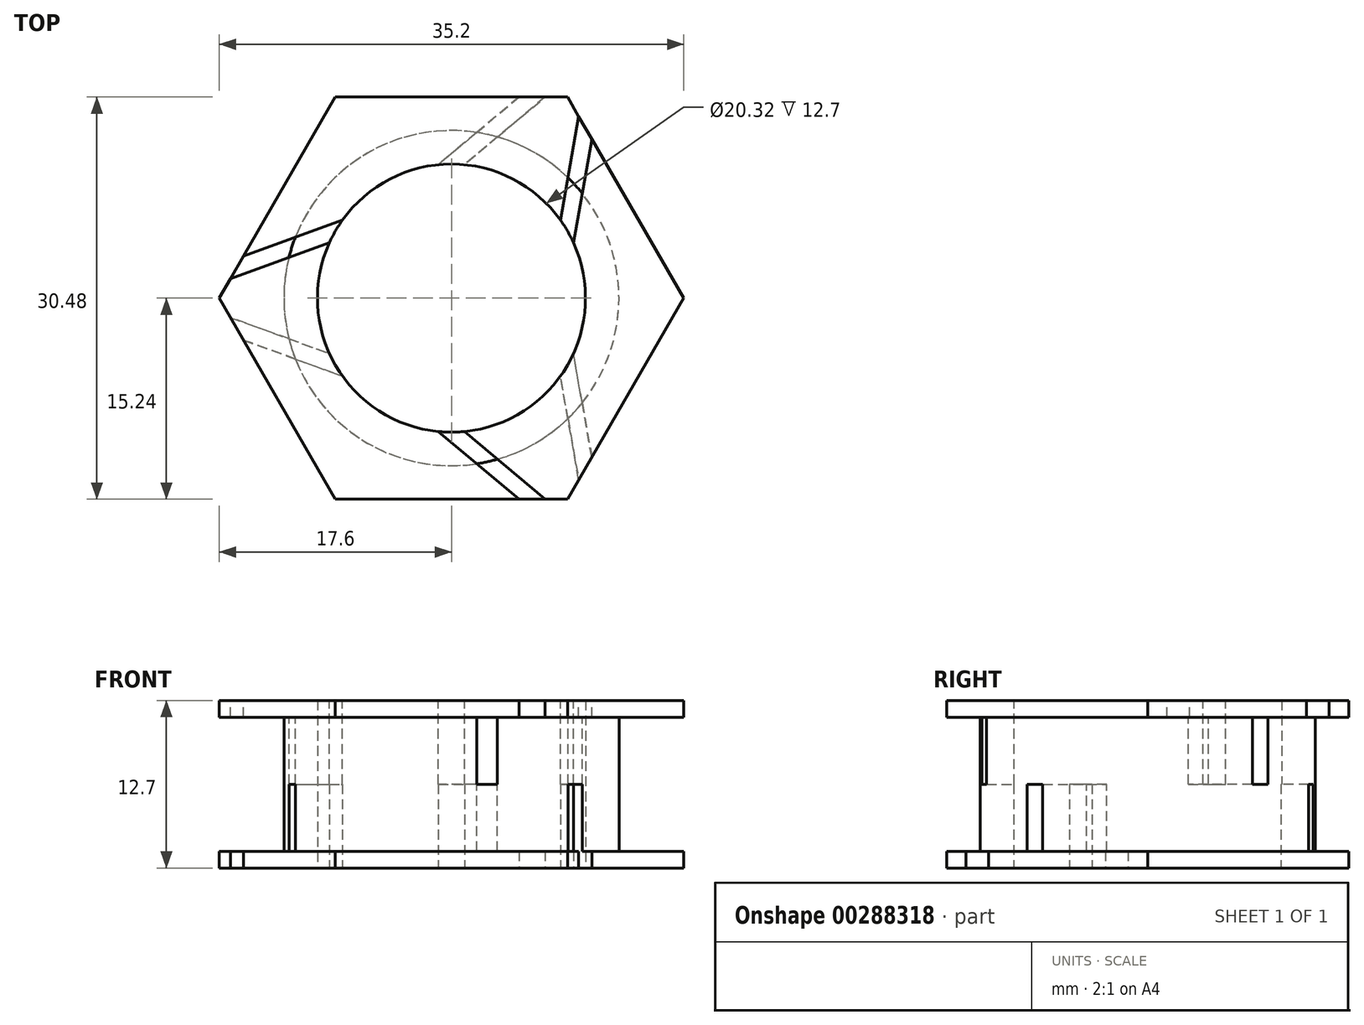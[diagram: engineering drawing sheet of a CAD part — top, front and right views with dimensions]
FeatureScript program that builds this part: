
annotation { "Feature Type Name" : "Feature", "Feature Type Description" : "" }
export const myFeature = defineFeature(function(context is Context, id is Id, definition is map)
    precondition{}
    {
        {
            var Q0;
            Q0=qCreatedBy(makeId("Top.planeOp"),FACE);
            var sketch = newSketch(context, id + "F0", { "sketchPlane" : qUnion([Q0])});
            skPoint(sketch, "E0.0.midPoint", {"position": v(8.96, 12.33) * mm});
            skCircle(sketch, "E1", {"center": v(0, 0) * mm, "radius": 10.16 * mm});
            skCircle(sketch, "E2", {"center": v(0, 0) * mm, "radius": 12.7 * mm});
            skCircle(sketch, "E3.cCircle", {"center": v(0, 0) * mm, "radius": 15.24 * mm, "construction": true});
            skLineSegment(sketch, "E3.0", {"start": v(8.8, 15.24) * mm, "end": v(17.6, 0) * mm});
            skLineSegment(sketch, "E3.1", {"start": v(17.6, 0) * mm, "end": v(8.8, -15.24) * mm});
            skLineSegment(sketch, "E3.2", {"start": v(8.8, -15.24) * mm, "end": v(-8.8, -15.24) * mm});
            skLineSegment(sketch, "E3.3", {"start": v(-8.8, -15.24) * mm, "end": v(-17.6, 0) * mm});
            skLineSegment(sketch, "E3.4", {"start": v(-17.6, 0) * mm, "end": v(-8.8, 15.24) * mm});
            skLineSegment(sketch, "E3.5", {"start": v(-8.8, 15.24) * mm, "end": v(8.8, 15.24) * mm});
            skPoint(sketch, "E3.0.midPoint", {"position": v(13.2, 7.62) * mm});
            skLineSegment(sketch, "E4", {"start": v(0, 0) * mm, "end": v(0, 15.24) * mm, "construction": true});
            skSolve(sketch);
        }
        {
            var Q0;
            Q0 = qSketchRegion(id + "F0", true);
            var Q1;
            Q1=makeQuery(id+"F0.imprint","IMPRINT",FACE,{"disambiguationData":[TD([[makeQuery(id+"F0.imprint","IMPRINT",EDGE,{"derivedFrom":sQuery(id+"F0.wireOp",EDGE,"E1")}),-1.0]])]});
            extrude(context, id + "F1", {"entities" : qUnion([Q0, Q1]), "endBound" : BoundingType.SYMMETRIC, "depth" : 12.7 * mm});
        }
        {
            var Q0;
            Q0=qCreatedBy(makeId("Top.planeOp"),FACE);
            var sketch = newSketch(context, id + "F2", { "sketchPlane" : qUnion([Q0])});
            skCircle(sketch, "E5.0", {"center": v(0, 0) * mm, "radius": 12.7 * mm});
            skCircle(sketch, "E6", {"center": v(0, 0) * mm, "radius": 17.6 * mm});
            skSolve(sketch);
        }
        {
            var Q0;
            Q0 = qSketchRegion(id + "F2", true);
            extrude(context, id + "F3", {"entities" : qUnion([Q0]), "operationType" : NewBodyOperationType.REMOVE, "endBound" : BoundingType.SYMMETRIC, "oppositeDirection" : true, "depth" : 10.16 * mm});
        }
        {
            var Q0;
            Q0=makeQuery(id+"F1.opExtrude","CAP_FACE",FACE,{"disambiguationData":[OSD([sQuery(id+"F0.wireOp",EDGE,"E0.0"),sQuery(id+"F0.wireOp",EDGE,"E0.1"),sQuery(id+"F0.wireOp",EDGE,"E0.2"),sQuery(id+"F0.wireOp",EDGE,"E0.3"),sQuery(id+"F0.wireOp",EDGE,"E0.4"),sQuery(id+"F0.wireOp",EDGE,"E1")])],"isStart":false});
            var sketch = newSketch(context, id + "F4", { "sketchPlane" : qUnion([Q0])});
            skLineSegment(sketch, "E7", {"start": v(-15.76, 3.18) * mm, "end": v(-8.26, 5.91) * mm});
            skLineSegment(sketch, "E8", {"start": v(-16.75, 1.47) * mm, "end": v(-9.25, 4.2) * mm});
            skLineSegment(sketch, "E9", {"start": v(0, 0) * mm, "end": v(-13.2, 7.62) * mm, "construction": true});
            skLineSegment(sketch, "E10.1.0", {"start": v(7.1, -15.24) * mm, "end": v(0.99, -10.11) * mm});
            skLineSegment(sketch, "E10.1.1", {"start": v(5.12, -15.24) * mm, "end": v(-0.99, -10.11) * mm});
            skLineSegment(sketch, "E10.2.0", {"start": v(9.65, 13.77) * mm, "end": v(8.26, 5.91) * mm});
            skLineSegment(sketch, "E10.2.1", {"start": v(10.64, 12.06) * mm, "end": v(9.25, 4.2) * mm});
            skPoint(sketch, "E10.center", {"position": v(0, 0) * mm});
            skSolve(sketch);
        }
        {
            var Q0;
            {var subQ0=sQuery(id+"F4.wireOp",EDGE,"E7");Q0=makeQuery(id+"F4.imprint","IMPRINT",FACE,{"disambiguationData":[TD([[makeQuery(id+"F4.imprint","IMPRINT",EDGE,{"derivedFrom":subQ0}),-1.0]])]});}
            var Q1;
            {var subQ0=sQuery(id+"F4.wireOp",EDGE,"E10.1.0");Q1=makeQuery(id+"F4.imprint","IMPRINT",FACE,{"disambiguationData":[TD([[makeQuery(id+"F4.imprint","IMPRINT",EDGE,{"derivedFrom":subQ0}),1.0]])]});}
            var Q2;
            {var subQ0=sQuery(id+"F4.wireOp",EDGE,"E10.2.0");Q2=makeQuery(id+"F4.imprint","IMPRINT",FACE,{"disambiguationData":[TD([[makeQuery(id+"F4.imprint","IMPRINT",EDGE,{"derivedFrom":subQ0}),1.0]])]});}
            extrude(context, id + "F5", {"entities" : qUnion([Q0, Q1, Q2]), "operationType" : NewBodyOperationType.REMOVE, "oppositeDirection" : true, "depth" : 6.35 * mm});
        }
        {
            var Q0;
            Q0=makeQuery(id+"F1.opExtrude","CAP_FACE",FACE,{"disambiguationData":[OSD([sQuery(id+"F0.wireOp",EDGE,"E1"),sQuery(id+"F0.wireOp",EDGE,"E3.0"),sQuery(id+"F0.wireOp",EDGE,"E3.1"),sQuery(id+"F0.wireOp",EDGE,"E3.2"),sQuery(id+"F0.wireOp",EDGE,"E3.3"),sQuery(id+"F0.wireOp",EDGE,"E3.4"),sQuery(id+"F0.wireOp",EDGE,"E3.5")])],"isStart":true});
            var sketch = newSketch(context, id + "F6", { "sketchPlane" : qUnion([Q0])});
            skLineSegment(sketch, "E11", {"start": v(0, 0) * mm, "end": v(-13.2, 7.62) * mm, "construction": true});
            skLineSegment(sketch, "E12", {"start": v(-15.76, 3.18) * mm, "end": v(-8.26, 5.91) * mm});
            skLineSegment(sketch, "E13", {"start": v(-16.75, 1.47) * mm, "end": v(-9.25, 4.2) * mm});
            skLineSegment(sketch, "E14.1.0", {"start": v(5.12, -15.24) * mm, "end": v(-0.99, -10.11) * mm});
            skLineSegment(sketch, "E14.1.1", {"start": v(7.1, -15.24) * mm, "end": v(0.99, -10.11) * mm});
            skLineSegment(sketch, "E14.2.0", {"start": v(10.64, 12.06) * mm, "end": v(9.25, 4.2) * mm});
            skLineSegment(sketch, "E14.2.1", {"start": v(9.65, 13.77) * mm, "end": v(8.26, 5.91) * mm});
            skPoint(sketch, "E14.center", {"position": v(0, 0) * mm});
            skSolve(sketch);
        }
        {
            var Q0;
            {var subQ0=sQuery(id+"F6.wireOp",EDGE,"E14.2.0");Q0=makeQuery(id+"F6.imprint","IMPRINT",FACE,{"disambiguationData":[TD([[makeQuery(id+"F6.imprint","IMPRINT",EDGE,{"derivedFrom":subQ0}),-1.0]])]});}
            var Q1;
            {var subQ0=sQuery(id+"F6.wireOp",EDGE,"E12");Q1=makeQuery(id+"F6.imprint","IMPRINT",FACE,{"disambiguationData":[TD([[makeQuery(id+"F6.imprint","IMPRINT",EDGE,{"derivedFrom":subQ0}),-1.0]])]});}
            var Q2;
            {var subQ0=sQuery(id+"F6.wireOp",EDGE,"E14.1.0");Q2=makeQuery(id+"F6.imprint","IMPRINT",FACE,{"disambiguationData":[TD([[makeQuery(id+"F6.imprint","IMPRINT",EDGE,{"derivedFrom":subQ0}),-1.0]])]});}
            extrude(context, id + "F7", {"entities" : qUnion([Q0, Q1, Q2]), "operationType" : NewBodyOperationType.REMOVE, "oppositeDirection" : true, "depth" : 6.35 * mm});
        }
    });
